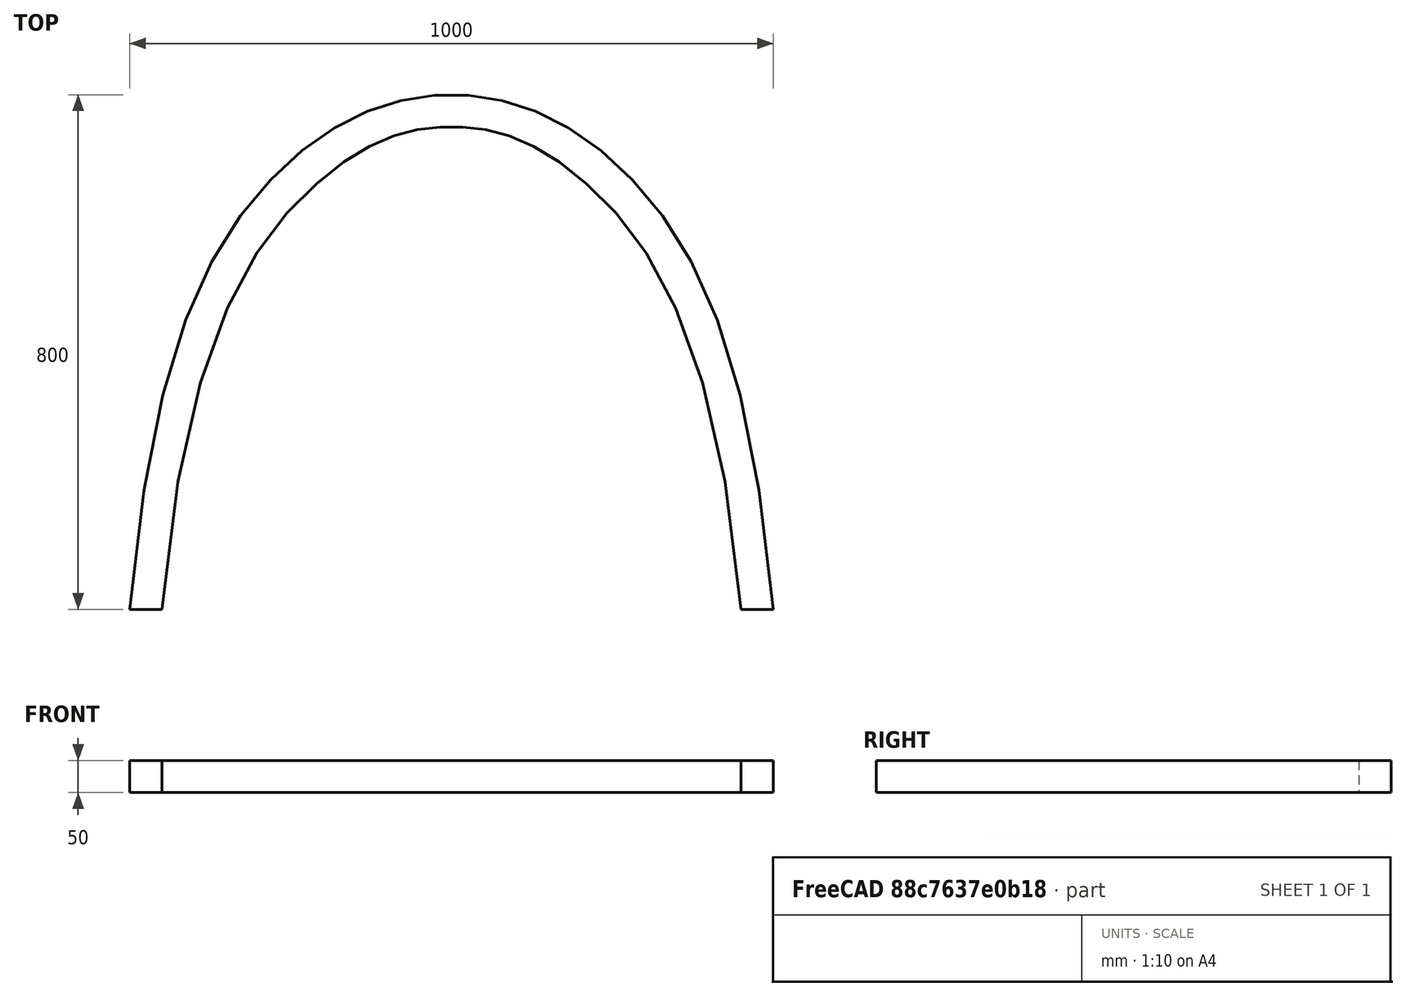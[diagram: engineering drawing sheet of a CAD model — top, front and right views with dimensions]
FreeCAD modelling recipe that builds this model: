
FCSTD DOCUMENT  (FreeCAD 1.0R38642 (Git))
Label: arc
License: All rights reserved
LicenseURL: https://en.wikipedia.org/wiki/All_rights_reserved
objects: Sketcher::SketchObject×1, PartDesign::Pad×1, PartDesign::Body×1, Fem::ConstraintFixed×1, Fem::ConstraintDisplacement×1, Fem::FemMeshShapeNetgenObject×1, Fem::FemSolverObjectPython×1, App::MaterialObjectPython×1, Fem::ConstraintForce×1, Fem::FemAnalysis×1
note: 6 computed .brp shape members not serialized (recipe doc carries the construction recipe); baked Part::Feature solids carry a one-line shape summary decoded from their .brp

FEATURE [Sketcher::SketchObject] Sketch
  ArcFitTolerance = 1e-06
  AttachmentSupport = -> [XY_Plane]
  FullyConstrained = false
  MakeInternals = false
  MapMode = 5
  sketch-geometry (28):
    g0-g6: Circle [constr] x7 (B-spline internal-alignment scaffolding for g7; pole/knot coordinates omitted)
    g7: BSplineCurve PolesCount=7 KnotsCount=5 Degree=3 IsPeriodic=0
    g8-g12: GeomPoint [constr] x5 (B-spline internal-alignment scaffolding for g7; pole/knot coordinates omitted)
    g13-g19: Circle [constr] x7 (B-spline internal-alignment scaffolding for g20; pole/knot coordinates omitted)
    g20: BSplineCurve PolesCount=7 KnotsCount=5 Degree=3 IsPeriodic=0
    g21-g25: GeomPoint [constr] x5 (B-spline internal-alignment scaffolding for g20; pole/knot coordinates omitted)
    g26: LineSegment StartX=-500 StartY=0 StartZ=0 EndX=-450 EndY=0 EndZ=0
    g27: LineSegment StartX=450 StartY=0 StartZ=0 EndX=500 EndY=0 EndZ=0
  constraints (22):
    c: Weight(g0) = 1
    c: Equal(g0, g1-g6) x6
    c: InternalAlignment(g0-g6 -> g7) x7
    c: InternalAlignment(g8-g12 -> g7) x5
    c: PointOnObject(g0,g-1)
    c: PointOnObject(g3,g-2)
    c: Symmetric(g1,g5,g-2)
    c: Symmetric(g2,g4,g-2)
    c: Symmetric(g7,g7,g-2)
    c: Distance(g10,g-1) = 750
    c: DistanceX(g7,g-1) = 450
    c: Weight(g13) = 1
    c: Equal(g13, g14-g19) x6
    c: InternalAlignment(g13-g19 -> g20) x7
    c: InternalAlignment(g21-g25 -> g20) x5
    c: PointOnObject(g13,g-1)
    c: PointOnObject(g16,g-2)
    c: Symmetric(g14,g18,g-2)
    c: Symmetric(g15,g17,g-2)
    c: Symmetric(g20,g20,g-2)
    c: Distance(g23,g-1) = 800
    c: DistanceX(g20,g-1) = 500
FEATURE [PartDesign::Pad] Pad
  Direction = (0,0,1)
  Length = 50
  Length2 = 10
  Profile = -> Sketch
  ReferenceAxis = -> Sketch [N_Axis]
  Refine = true
  Suppressed = false
  Type = 0
FEATURE [PartDesign::Body] Body
  AllowCompound = false
  Group = -> [Sketch,Pad]
  Origin = -> Origin
  Tip = -> Pad
FEATURE [Fem::ConstraintFixed] ConstraintFixed
  NormalDirection = (0,-1,0)
  Normals = (16) [(0,-1,0),(0,-1,0),(0,-1,0),(0,-1,0),(0,-1,0),(0,-1,0),(0,-1,0),(0,-1,0),(0,-1,0),(0,-1,0),(0,-1,0),(0,-1,0),(0,-1,0),(0,-1,0),(0,-1,0),(0,-1,0)]
  Points = (16) [(-500,0,50),(-483.333,0,50),(-466.667,0,50),(-450,0,50),(-500,0,33.3333),(-483.333,0,33.3333),(-466.667,0,33.3333),(-450,0,33.3333),(-500,0,16.6667),+7 more]
  References = -> [Pad]
  Suppressed = false
FEATURE [Fem::ConstraintDisplacement] ConstraintDisplacement
  NormalDirection = (0,-1,0)
  Normals = (16) [(0,-1,0),(0,-1,0),(0,-1,0),(0,-1,0),(0,-1,0),(0,-1,0),(0,-1,0),(0,-1,0),(0,-1,0),(0,-1,0),(0,-1,0),(0,-1,0),(0,-1,0),(0,-1,0),(0,-1,0),(0,-1,0)]
  Points = (16) [(450,0,50),(466.667,0,50),(483.333,0,50),(500,0,50),(450,0,33.3333),(466.667,0,33.3333),(483.333,0,33.3333),(500,0,33.3333),(450,0,16.6667),+7 more]
  References = -> [Pad]
  Suppressed = true
  hasXFormula = false
  hasYFormula = false
  hasZFormula = false
  rotxFree = true
  rotyFree = true
  rotzFree = true
  useFlowSurfaceForce = false
  xDisplacement = 100
  xFree = false
  xRotation = 0
  yDisplacement = 0
  yFree = true
  yRotation = 0
  zDisplacement = 0
  zFree = true
  zRotation = 0
FEATURE [Fem::FemMeshShapeNetgenObject] FEMMeshNetgen
  Fineness = 4
  GrowthRate = 0.3
  MaxSize = 10
  MinSize = 0
  NbSegsPerEdge = 1
  NbSegsPerRadius = 2
  Optimize = true
  SecondOrder = true
  Shape = -> Pad
FEATURE [Fem::FemSolverObjectPython] SolverCcxTools  # FEM object (typed FeaturePython)
  AnalysisType = 0
  BeamReducedIntegration = true
  BeamShellResultOutput3D = true
  BucklingFactors = 1
  EigenmodeHighLimit = 1000000
  EigenmodeLowLimit = 0
  EigenmodesCount = 10
  GeometricalNonlinearity = 0
  IterationsControlParameterCutb = 0.25,0.5,0.75,0.85,,,1.5,
  IterationsControlParameterIter = 4,8,9,200,10,400,,200,,
  IterationsControlParameterTimeUse = false
  IterationsMaximum = 2000
  IterationsUserDefinedIncrementations = false
  IterationsUserDefinedTimeStepLength = false
  MaterialNonlinearity = 0
  MatrixSolverType = 0
  ModelSpace = 0
  OutputFrequency = 1
  SplitInputWriter = false
  ThermoMechSteadyState = true
  ThermoMechType = 0
  TimeEnd = 1
  TimeInitialStep = 1
  TimeMaximumStep = 1
  TimeMinimumStep = 1e-05
FEATURE [App::MaterialObjectPython] MaterialSolid  # material (typed FeaturePython)
  Category = 0
  Material = AmbientColor=(0.3000, 0.3000, 0.3000, 1.0),Author=Uwe Stöhr,CardName=Aluminum-Generic,Density=2.7e-06 kg/mm^3,+17 more (map truncated)
  References = -> [Pad]
FEATURE [Fem::ConstraintForce] ConstraintForce
  Direction = -> Pad [Edge10]
  DirectionVector = (1,0,0)
  Force = 15000000
  NormalDirection = (0,-1,0)
  Normals = (16) [(0,-1,0),(0,-1,0),(0,-1,0),(0,-1,0),(0,-1,0),(0,-1,0),(0,-1,0),(0,-1,0),(0,-1,0),(0,-1,0),(0,-1,0),(0,-1,0),(0,-1,0),(0,-1,0),(0,-1,0),(0,-1,0)]
  Points = (16) [(450,0,50),(466.667,0,50),(483.333,0,50),(500,0,50),(450,0,33.3333),(466.667,0,33.3333),(483.333,0,33.3333),(500,0,33.3333),(450,0,16.6667),+7 more]
  References = -> [Pad]
  Suppressed = false
FEATURE [Fem::FemAnalysis] Analysis
  Group = -> [ConstraintFixed,ConstraintDisplacement,FEMMeshNetgen,SolverCcxTools,MaterialSolid,ConstraintForce]
